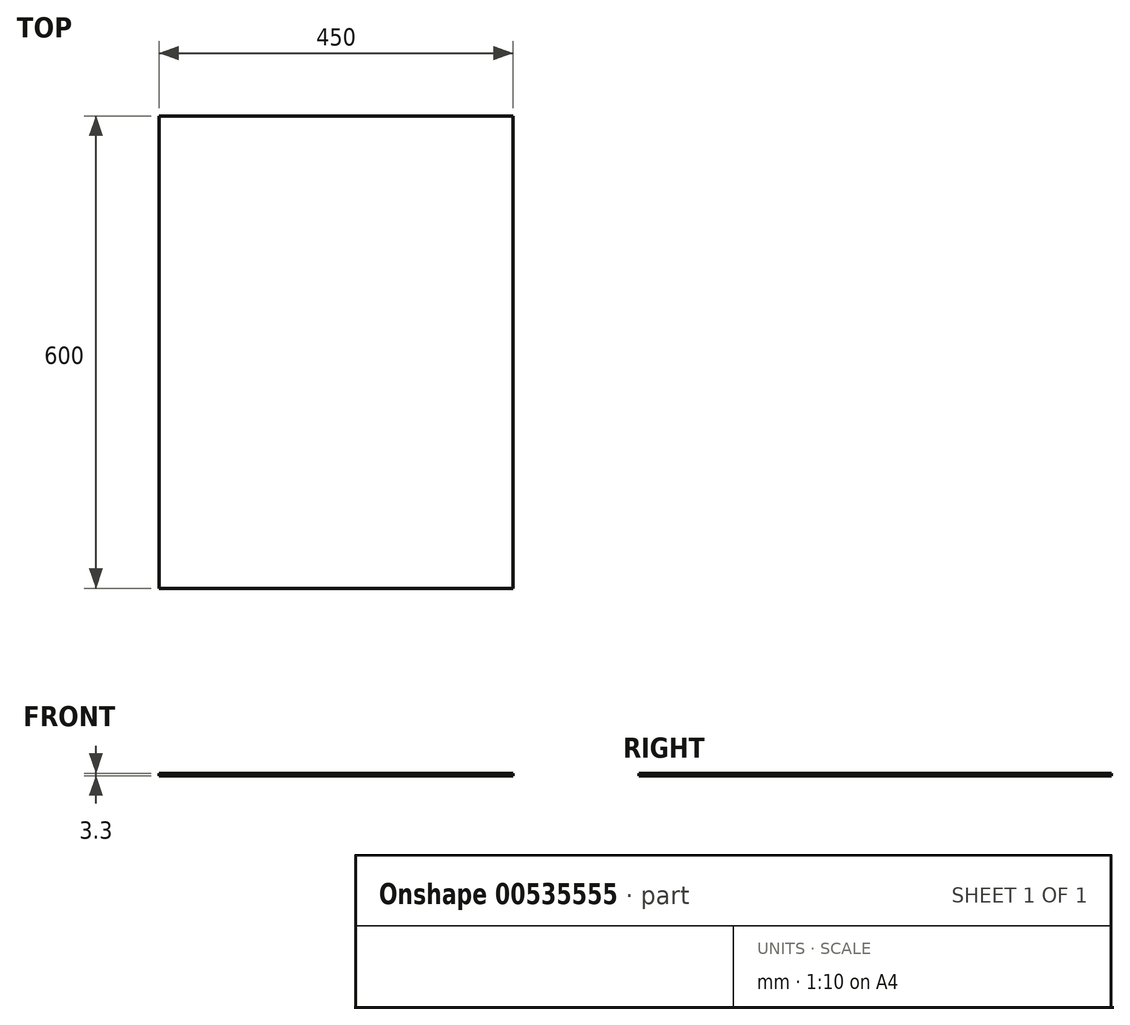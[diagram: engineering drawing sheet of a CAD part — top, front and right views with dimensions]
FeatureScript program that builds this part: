
annotation { "Feature Type Name" : "Feature", "Feature Type Description" : "" }
export const myFeature = defineFeature(function(context is Context, id is Id, definition is map)
    precondition{}
    {
        {
            var Q0;
            Q0=qCreatedBy(makeId("Top.planeOp"),FACE);
            var sketch = newSketch(context, id + "F0", { "sketchPlane" : qUnion([Q0])});
            skLineSegment(sketch, "E0.bottom", {"start": v(-225, 300) * mm, "end": v(225, 300) * mm});
            skLineSegment(sketch, "E0.top", {"start": v(-225, -300) * mm, "end": v(225, -300) * mm});
            skLineSegment(sketch, "E0.left", {"start": v(-225, 300) * mm, "end": v(-225, -300) * mm});
            skLineSegment(sketch, "E0.right", {"start": v(225, 300) * mm, "end": v(225, -300) * mm});
            skPoint(sketch, "E0.middle", {"position": v(0, 0) * mm});
            skSolve(sketch);
        }
        {
            var Q0;
            Q0 = qSketchRegion(id + "F0", true);
            extrude(context, id + "F1", {"entities" : qUnion([Q0]), "depth" : 3.3 * mm, "offsetDistance" : 25 * mm});
        }
    });
